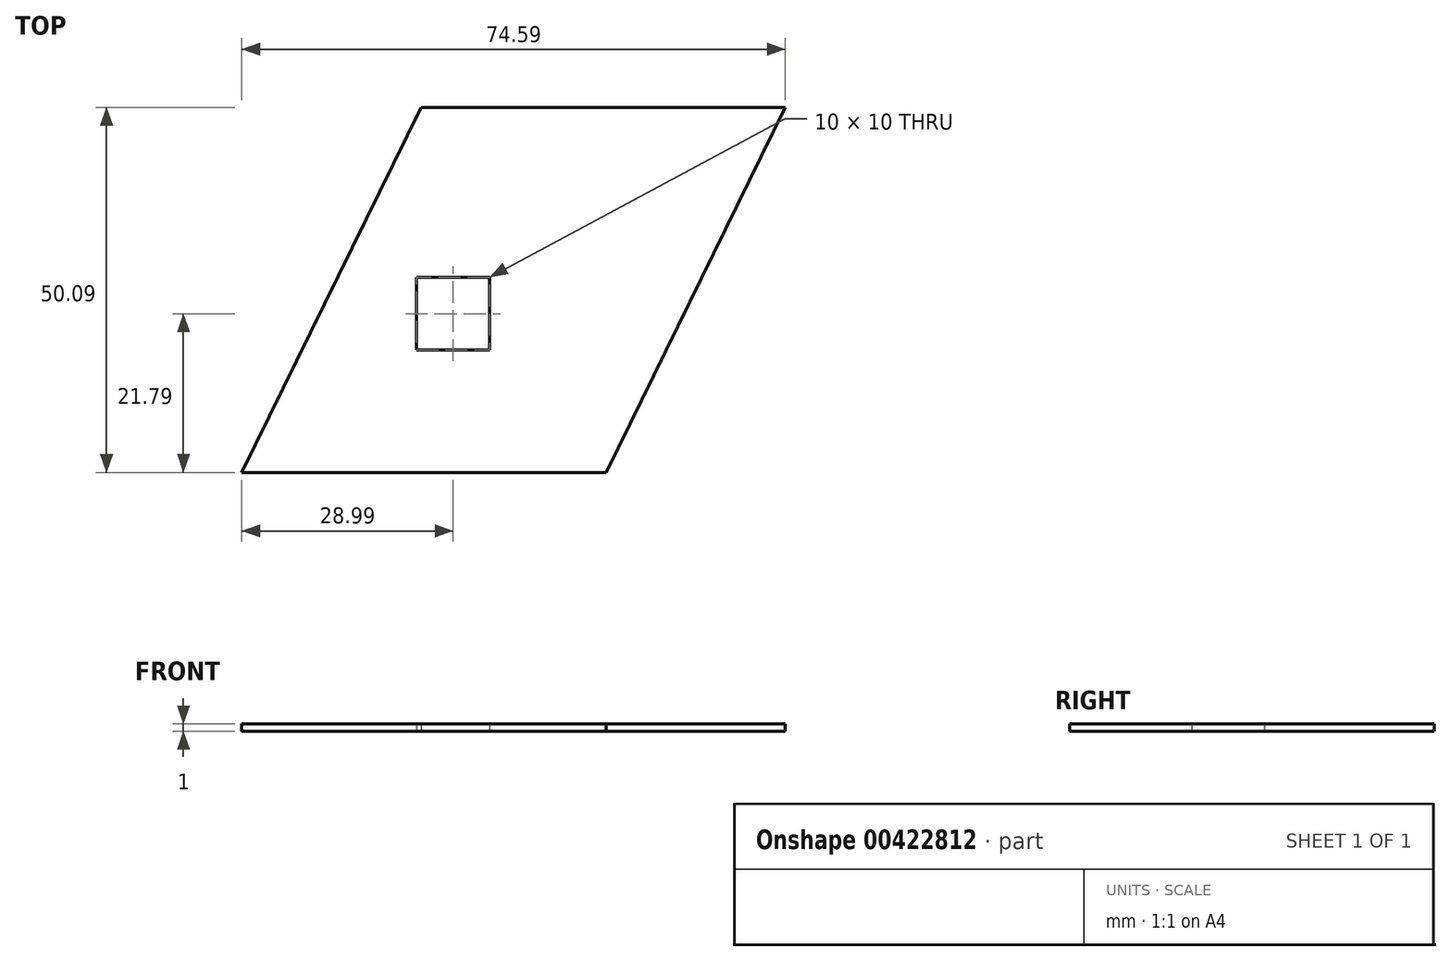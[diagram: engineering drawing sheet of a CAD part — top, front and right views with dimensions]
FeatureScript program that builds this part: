
annotation { "Feature Type Name" : "Feature", "Feature Type Description" : "" }
export const myFeature = defineFeature(function(context is Context, id is Id, definition is map)
    precondition{}
    {
        {
            var Q0;
            Q0=qCreatedBy(makeId("Top.planeOp"),FACE);
            var sketch = newSketch(context, id + "F0", { "sketchPlane" : qUnion([Q0])});
            skLineSegment(sketch, "E0", {"start": v(-38.1, 40.35) * mm, "end": v(11.9, 40.35) * mm});
            skLineSegment(sketch, "E1", {"start": v(11.9, 40.35) * mm, "end": v(-12.7, -9.74) * mm});
            skLineSegment(sketch, "E2", {"start": v(-12.7, -9.74) * mm, "end": v(-62.7, -9.74) * mm});
            skLineSegment(sketch, "E3", {"start": v(-62.7, -9.74) * mm, "end": v(-38.1, 40.35) * mm});
            skLineSegment(sketch, "E4.bottom", {"start": v(-38.7, 17.05) * mm, "end": v(-28.7, 17.05) * mm});
            skLineSegment(sketch, "E4.top", {"start": v(-38.7, 7.05) * mm, "end": v(-28.7, 7.05) * mm});
            skLineSegment(sketch, "E4.left", {"start": v(-38.7, 17.05) * mm, "end": v(-38.7, 7.05) * mm});
            skLineSegment(sketch, "E4.right", {"start": v(-28.7, 17.05) * mm, "end": v(-28.7, 7.05) * mm});
            skSolve(sketch);
        }
        {
            var Q0;
            Q0=makeQuery(id+"F0.imprint","IMPRINT",FACE,{"disambiguationData":[TD([[makeQuery(id+"F0.imprint","IMPRINT",EDGE,{"derivedFrom":sQuery(id+"F0.wireOp",EDGE,"E0")}),-1.0]])]});
            extrude(context, id + "F1", {"entities" : qUnion([Q0]), "depth" : mm});
        }
    });
